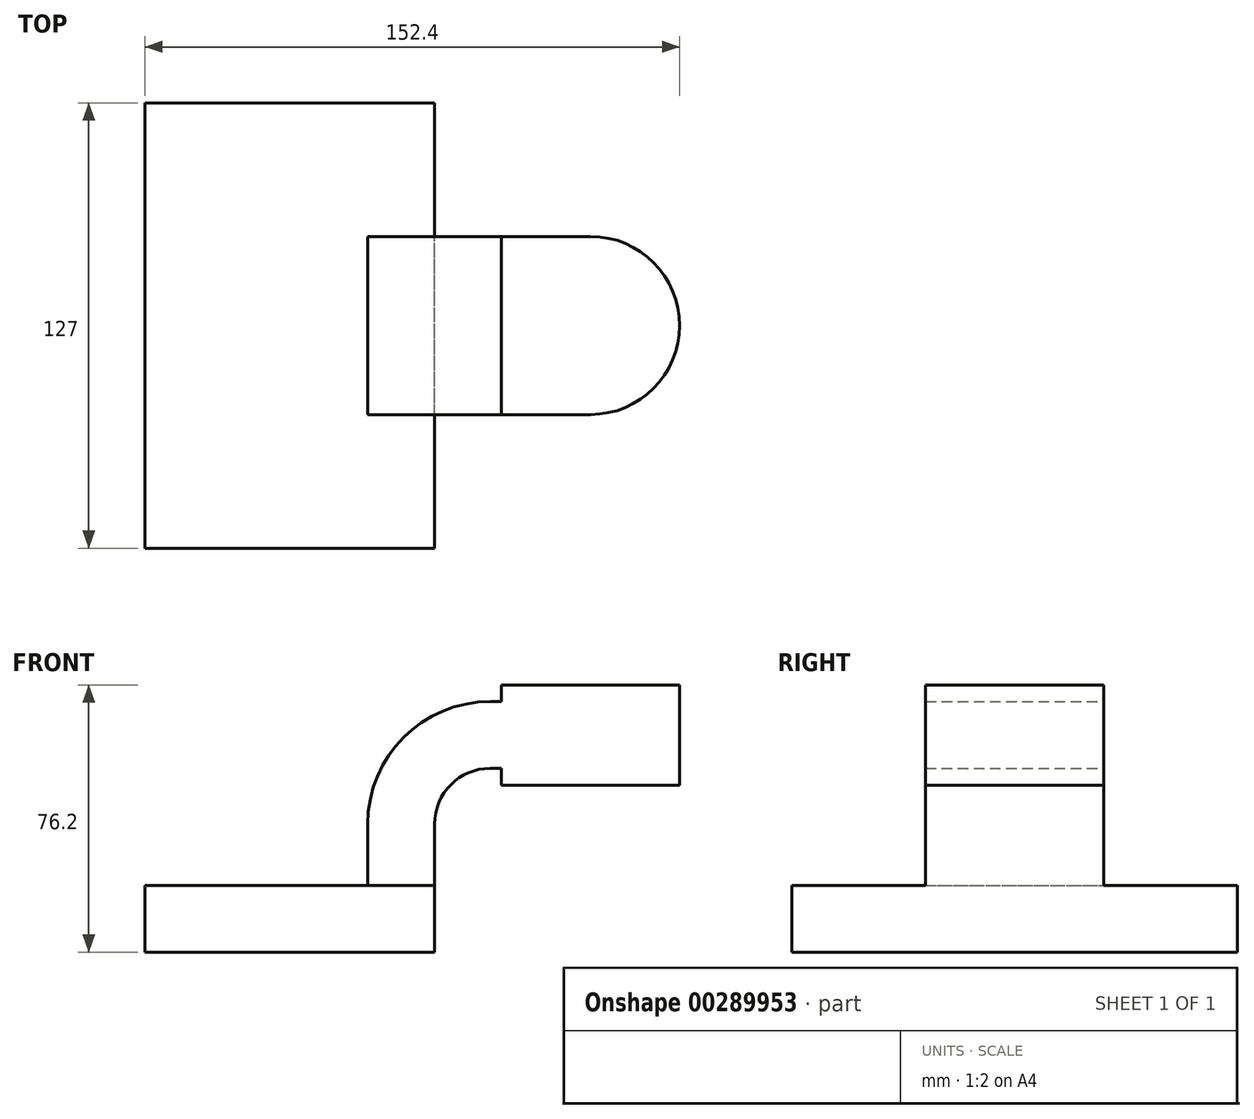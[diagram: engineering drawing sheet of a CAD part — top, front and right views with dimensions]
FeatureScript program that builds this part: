
annotation { "Feature Type Name" : "Feature", "Feature Type Description" : "" }
export const myFeature = defineFeature(function(context is Context, id is Id, definition is map)
    precondition{}
    {
        {
            var Q0;
            Q0=qCreatedBy(makeId("Front.planeOp"),FACE);
            var sketch = newSketch(context, id + "F0", { "sketchPlane" : qUnion([Q0])});
            skLineSegment(sketch, "E0.bottom", {"start": v(41.28, -9.53) * mm, "end": v(-41.28, -9.53) * mm});
            skLineSegment(sketch, "E0.top", {"start": v(41.28, 9.53) * mm, "end": v(-41.28, 9.52) * mm});
            skLineSegment(sketch, "E0.left", {"start": v(41.28, -9.53) * mm, "end": v(41.28, 9.52) * mm});
            skLineSegment(sketch, "E0.right", {"start": v(-41.28, -9.53) * mm, "end": v(-41.28, 9.52) * mm});
            skPoint(sketch, "E0.middle", {"position": v(0, 0) * mm});
            skLineSegment(sketch, "E1.bottom", {"start": v(111.12, 38.1) * mm, "end": v(60.33, 38.1) * mm});
            skLineSegment(sketch, "E1.top", {"start": v(111.12, 66.68) * mm, "end": v(60.33, 66.67) * mm});
            skLineSegment(sketch, "E1.left", {"start": v(111.12, 38.1) * mm, "end": v(111.12, 66.68) * mm});
            skLineSegment(sketch, "E1.right", {"start": v(60.33, 38.1) * mm, "end": v(60.33, 66.68) * mm});
            skPoint(sketch, "E1.middle", {"position": v(85.72, 52.39) * mm});
            skLineSegment(sketch, "E2", {"start": v(41.28, 9.53) * mm, "end": v(41.28, 27) * mm});
            skArc(sketch, "E3", {"start": v(41.28, 27) * mm, "mid": v(45.92, 38.23) * mm, "end": v(57.15, 42.88) * mm});
            skLineSegment(sketch, "E4", {"start": v(57.15, 42.88) * mm, "end": v(85.73, 42.88) * mm});
            skPoint(sketch, "E4.endSnap0", {"position": v(85.73, 38.1) * mm});
            skLineSegment(sketch, "E5.0", {"start": v(57.15, 61.93) * mm, "end": v(85.73, 61.93) * mm});
            skArc(sketch, "E5.1", {"start": v(22.23, 27) * mm, "mid": v(32.45, 51.7) * mm, "end": v(57.15, 61.93) * mm});
            skLineSegment(sketch, "E5.2", {"start": v(22.23, 9.53) * mm, "end": v(22.23, 27) * mm});
            skLineSegment(sketch, "E6", {"start": v(85.73, 38.1) * mm, "end": v(85.72, 66.67) * mm});
            skFitSpline(sketch, "E7", {"points": [v(-41.28, 9.52) * mm, v(57.15, 61.93) * mm], "startDerivative": vector(-0.98, 99.43) * mm, "endDerivative": vector(171.45, -7.66) * mm});
            skSolve(sketch);
        }
        {
            var Q0;
            Q0=makeQuery(id+"F0.imprint","IMPRINT",FACE,{"disambiguationData":[TD([[makeQuery(id+"F0.imprint","IMPRINT",EDGE,{"derivedFrom":sQuery(id+"F0.wireOp",EDGE,"E0.bottom")}),-1.0]])]});
            extrude(context, id + "F1", {"entities" : qUnion([Q0]), "endBound" : BoundingType.SYMMETRIC, "depth" : 127 * mm});
        }
        {
            var Q0;
            {var subQ1=sQuery(id+"F0.wireOp",EDGE,"E2");Q0=makeQuery(id+"F0.imprint","IMPRINT",FACE,{"disambiguationData":[TD([[makeQuery(id+"F0.imprint","IMPRINT",EDGE,{"derivedFrom":subQ1}),1.0]])]});}
            var Q1;
            {var subQ0=sQuery(id+"F0.wireOp",EDGE,"E4");var subQ1=sQuery(id+"F0.wireOp",EDGE,"E1.right");var subQ2=makeQuery(id+"F0.imprint","INTERSECT",VERTEX,{"derivedFrom":[subQ1,subQ0]});Q1=makeQuery(id+"F0.imprint","IMPRINT",FACE,{"disambiguationData":[TD([[makeQuery(id+"F0.imprint","IMPRINT",EDGE,{"disambiguationData":[TD([[subQ2,-1.0]])],"derivedFrom":subQ1}),-1.0]])]});}
            var Q2;
            {var subQ0=sQuery(id+"F0.wireOp",EDGE,"E1.right");var subQ1=sQuery(id+"F0.wireOp",EDGE,"E1.top");var subQ2=makeQuery(id+"F0.imprint","INTERSECT",VERTEX,{"derivedFrom":[subQ1,subQ0]});Q2=makeQuery(id+"F0.imprint","IMPRINT",FACE,{"disambiguationData":[TD([[makeQuery(id+"F0.imprint","IMPRINT",EDGE,{"disambiguationData":[TD([[subQ2,1.0]])],"derivedFrom":subQ1}),1.0]])]});}
            var Q3;
            {var subQ0=sQuery(id+"F0.wireOp",EDGE,"E1.right");var subQ1=sQuery(id+"F0.wireOp",EDGE,"E1.bottom");var subQ2=makeQuery(id+"F0.imprint","INTERSECT",VERTEX,{"derivedFrom":[subQ1,subQ0]});Q3=makeQuery(id+"F0.imprint","IMPRINT",FACE,{"disambiguationData":[TD([[makeQuery(id+"F0.imprint","IMPRINT",EDGE,{"disambiguationData":[TD([[subQ2,1.0]])],"derivedFrom":subQ1}),-1.0]])]});}
            extrude(context, id + "F2", {"entities" : qUnion([Q0, Q1, Q2, Q3]), "operationType" : NewBodyOperationType.ADD, "endBound" : BoundingType.SYMMETRIC, "depth" : 50.8 * mm});
        }
        {
            var Q0;
            Q0=makeQuery(id+"F0.imprint","IMPRINT",FACE,{"disambiguationData":[TD([[makeQuery(id+"F0.imprint","IMPRINT",EDGE,{"derivedFrom":sQuery(id+"F0.wireOp",EDGE,"E5.1")}),1.0]])]});
            extrude(context, id + "F3", {"entities" : qUnion([Q0]), "operationType" : NewBodyOperationType.ADD, "endBound" : BoundingType.SYMMETRIC, "depth" : 6.35 * mm});
        }
        {
            var Q0;
            {var subQ4=sQuery(id+"F0.wireOp",EDGE,"E1.left");Q0=makeQuery(id+"F0.imprint","IMPRINT",FACE,{"disambiguationData":[TD([[makeQuery(id+"F0.imprint","IMPRINT",EDGE,{"derivedFrom":subQ4}),1.0]])]});}
            var Q1;
            Q1=sQuery(id+"F0.wireOp",EDGE,"E6");
            revolve(context, id + "F4", {"operationType" : NewBodyOperationType.ADD, "entities" : qUnion([Q0]), "axis" : qUnion([Q1]), "revolveType" : RevolveType.FULL});
        }
    });
